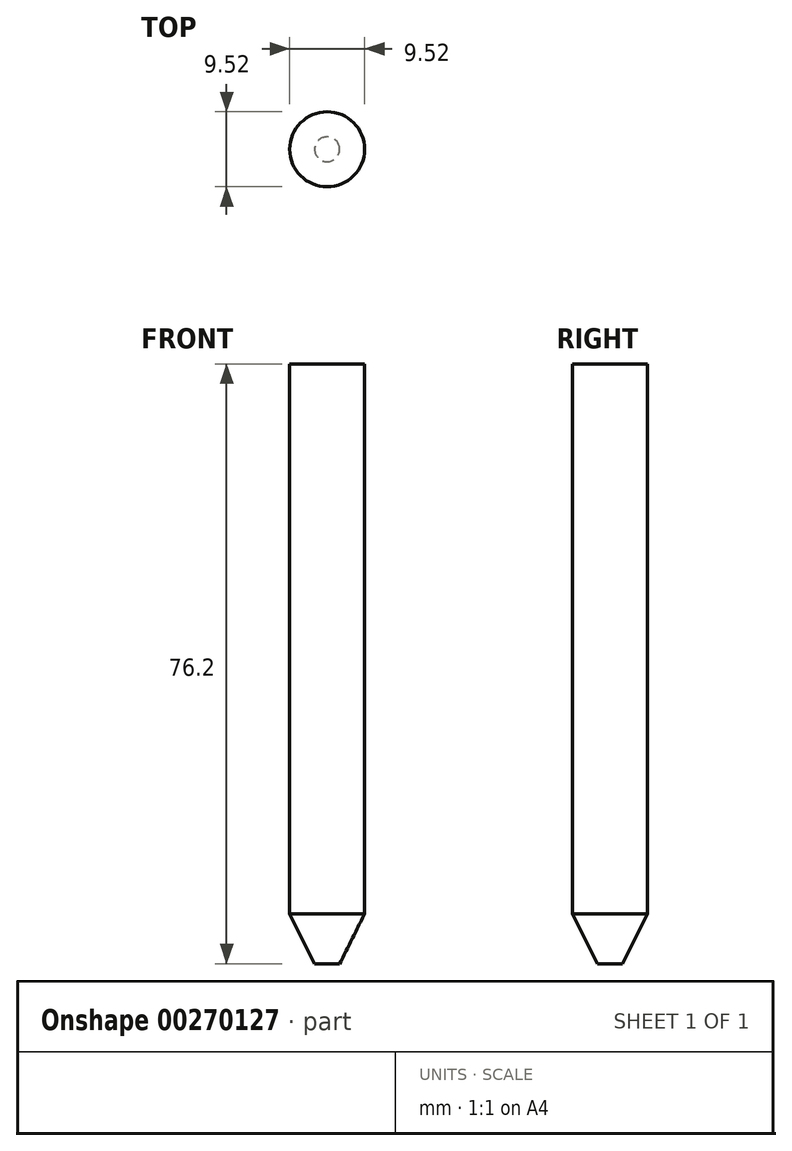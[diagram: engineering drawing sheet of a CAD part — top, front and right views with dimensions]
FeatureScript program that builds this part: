
annotation { "Feature Type Name" : "Feature", "Feature Type Description" : "" }
export const myFeature = defineFeature(function(context is Context, id is Id, definition is map)
    precondition{}
    {
        {
            var Q0;
            Q0=qCreatedBy(makeId("Top.planeOp"),FACE);
            var sketch = newSketch(context, id + "F0", { "sketchPlane" : qUnion([Q0])});
            skCircle(sketch, "E0", {"center": v(0, 0) * mm, "radius": 1.59 * mm});
            skSolve(sketch);
        }
        {
            var Q0;
            Q0=qCreatedBy(makeId("Top.planeOp"),FACE);
            cPlane(context, id + "F1", {"entities" : qUnion([Q0]), "cplaneType" : CPlaneType.OFFSET, "offset" : 6.35 * mm, "width" : 152.4 * mm, "height" : 152.4 * mm});
        }
        {
            var Q0;
            Q0=qCreatedBy(id+"F1.planeOp",FACE);
            var sketch = newSketch(context, id + "F2", { "sketchPlane" : qUnion([Q0])});
            skCircle(sketch, "E1", {"center": v(0, 0) * mm, "radius": 4.76 * mm});
            skSolve(sketch);
        }
        {
            var Q0;
            Q0=qCreatedBy(makeId("Top.planeOp"),FACE);
            cPlane(context, id + "F3", {"entities" : qUnion([Q0]), "cplaneType" : CPlaneType.OFFSET, "offset" : 76.2 * mm, "width" : 152.4 * mm, "height" : 152.4 * mm});
        }
        {
            var Q0;
            Q0=qCreatedBy(id+"F3.planeOp",FACE);
            var sketch = newSketch(context, id + "F4", { "sketchPlane" : qUnion([Q0])});
            skCircle(sketch, "E2", {"center": v(0, 0) * mm, "radius": 4.76 * mm});
            skSolve(sketch);
        }
        {
            var Q0;
            Q0 = qSketchRegion(id + "F0", true);
            var Q1;
            Q1 = qSketchRegion(id + "F2", true);
            loft(context, id + "F5", {"sheetProfilesArray" : [{ "sheetProfileEntities" : qUnion([Q0]) }, { "sheetProfileEntities" : qUnion([Q1]) }]});
        }
        {
            var Q1;
            Q1 = qSketchRegion(id + "F2", true);
            var Q2;
            Q2 = qSketchRegion(id + "F4", true);
            loft(context, id + "F6", {"operationType" : NewBodyOperationType.ADD, "sheetProfilesArray" : [{ "sheetProfileEntities" : qUnion([Q1]) }, { "sheetProfileEntities" : qUnion([Q2]) }]});
        }
    });
